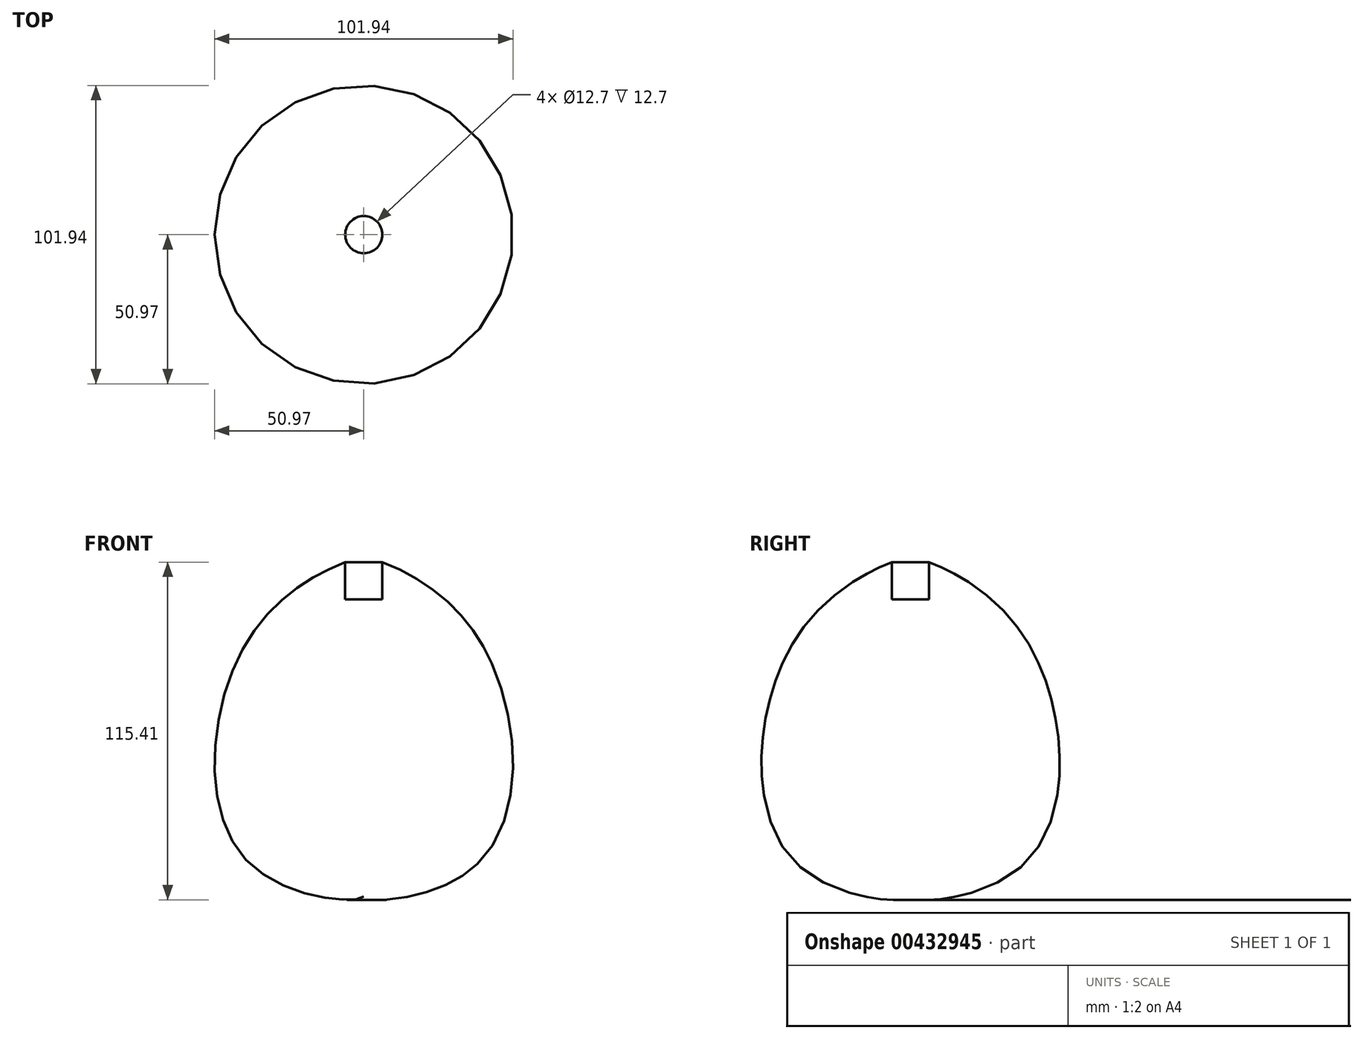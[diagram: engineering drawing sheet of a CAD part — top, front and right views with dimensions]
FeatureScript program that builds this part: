
annotation { "Feature Type Name" : "Feature", "Feature Type Description" : "" }
export const myFeature = defineFeature(function(context is Context, id is Id, definition is map)
    precondition{}
    {
        {
            var Q0;
            Q0=qCreatedBy(makeId("Front.planeOp"),FACE);
            var sketch = newSketch(context, id + "F0", { "sketchPlane" : qUnion([Q0])});
            skLineSegment(sketch, "E0", {"start": v(0, -50.8) * mm, "end": v(0, 50.8) * mm});
            skFitSpline(sketch, "E1", {"points": [v(-6.35, 63.5) * mm, v(-42.9, 30.76) * mm, v(-38.66, -39.86) * mm, v(0, -50.8) * mm], "startDerivative": vector(-125.72, -48.85) * mm, "endDerivative": vector(28.45, 28.1) * mm});
            skLineSegment(sketch, "E2", {"start": v(-50.8, 0) * mm, "end": v(0, 0) * mm, "construction": true});
            skLineSegment(sketch, "E3", {"start": v(0, 50.8) * mm, "end": v(-6.35, 50.8) * mm});
            skLineSegment(sketch, "E4", {"start": v(-6.35, 50.8) * mm, "end": v(-6.35, 63.5) * mm});
            skSolve(sketch);
        }
        {
            var Q0;
            Q0=makeQuery(id+"F0.imprint","IMPRINT",FACE,{"disambiguationData":[TD([[makeQuery(id+"F0.imprint","IMPRINT",EDGE,{"derivedFrom":sQuery(id+"F0.wireOp",EDGE,"E0")}),1.0]])]});
            var Q1;
            Q1=sQuery(id+"F0.wireOp",EDGE,"E0");
            revolve(context, id + "F1", {"entities" : qUnion([Q0]), "axis" : qUnion([Q1]), "revolveType" : RevolveType.FULL});
        }
    });
